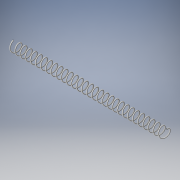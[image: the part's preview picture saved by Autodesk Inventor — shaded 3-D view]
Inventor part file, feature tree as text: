
AUTODESK INVENTOR PART (.ipt)
format: ipt  version: 2018.3 (Build 223284000, 284)  size: 349,184 bytes
history: native  units: in
note: dims shown in document units (in); Inventor stores cm internally (conversion verified against a paired STEP export)
features: helix x1, sketch x1
ambient origin geometry x8: Origin, YZ Plane, XZ Plane, XY Plane, X Axis, Y Axis, Z Axis, Center Point
bodies: Solid1 (feature_tree)
feature tree (2):
  helix  "Coil1"  [1 undecoded]
  sketch  "Sketch1"  dims[d1=0.043in d3=0.215in d4=1.0in d5=6.55in d6=11.811in d7=0.0in d8=90.0deg d9=90.0deg d10=0.0in d11=0.0in]
note: 1 required parameter value undecoded (feature->parameter linkage not recoverable at this tier; creation-order binding heuristic only, values carry confidence <= 0.55)
